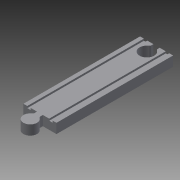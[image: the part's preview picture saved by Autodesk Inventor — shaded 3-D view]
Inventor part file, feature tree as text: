
AUTODESK INVENTOR PART (.ipt)
format: ipt  version: 2015 (Build 190159000, 159)  size: 125,952 bytes
history: native  units: in
note: dims shown in document units (in); Inventor stores cm internally (conversion verified against a paired STEP export)
features: extrude x2, sketch x2, fillet x1
ambient origin geometry x8: Origin, YZ Plane, XZ Plane, XY Plane, X Axis, Y Axis, Z Axis, Center Point
bodies: Solid1 (feature_tree)
feature tree (5):
  extrude  "Extrusion1"  Depth=0.75in
  extrude  "Extrusion2"  Depth=1.0in
  fillet  "Fillet1"  Radius=1.0in
  sketch  "Sketch1"  dims[d0=3.4in d1=0.75in]
  sketch  "Sketch2"  dims[d2=0.7in d3=1.0in d4=1.0in d5=12.0in d6=12.0in d7=0.0in d8=1.375in d9=2.025in d10=1.7in d13=1.7in d16=0.6in d17=0.3in d18=1.0in d19=0.0in d21=0.4in d22=0.75in d23=2.65in d24=3.0in d25=0.1875in d26=0.0in d27=0.19in]
